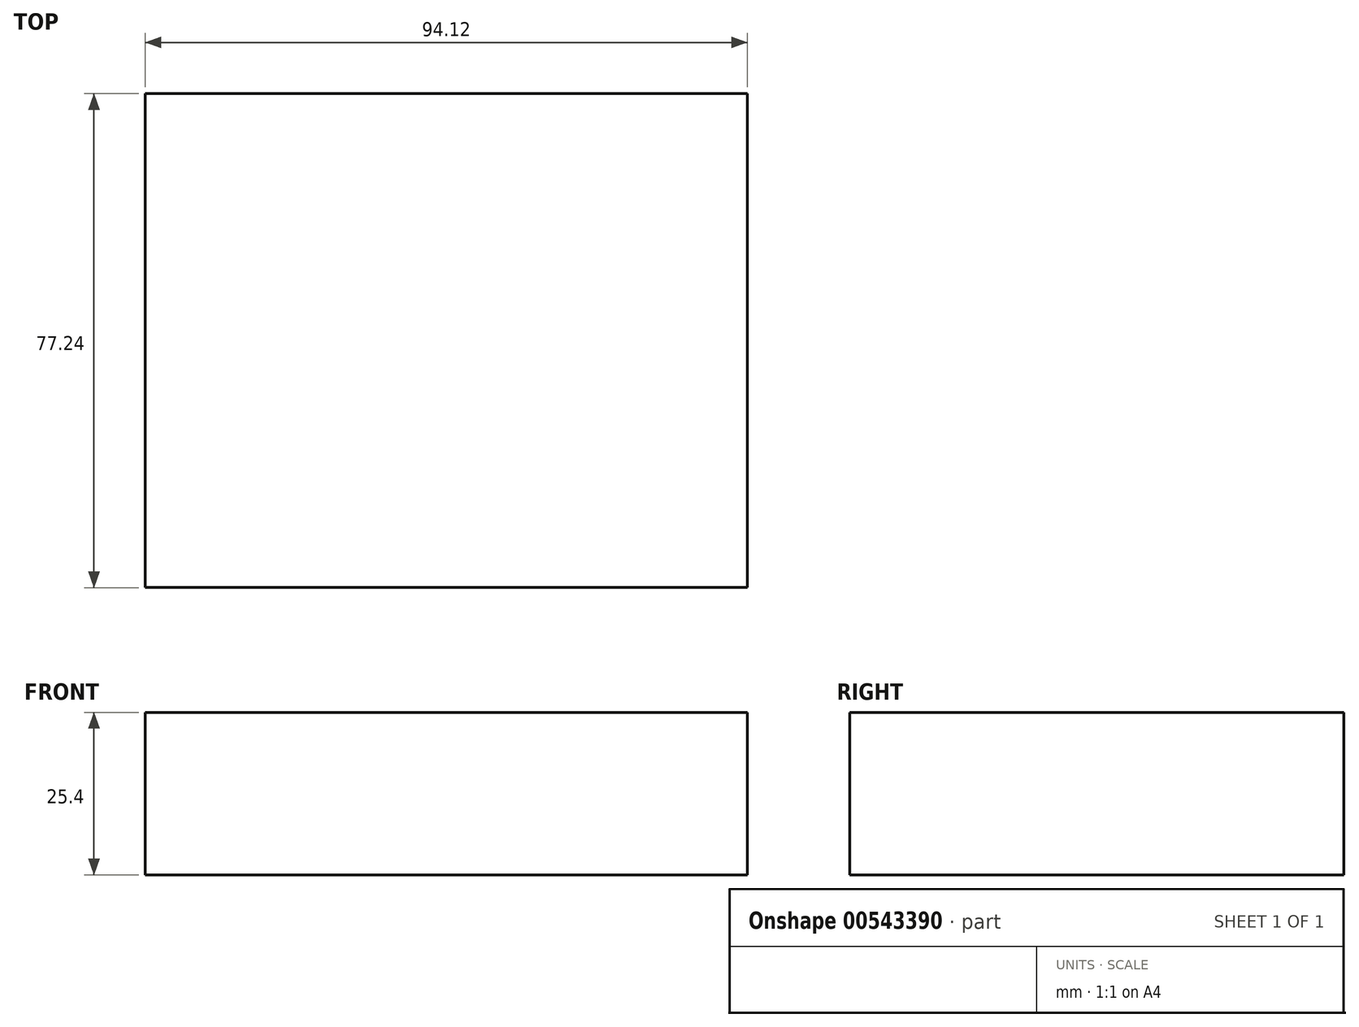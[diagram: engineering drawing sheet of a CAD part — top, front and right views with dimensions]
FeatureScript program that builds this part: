
annotation { "Feature Type Name" : "Feature", "Feature Type Description" : "" }
export const myFeature = defineFeature(function(context is Context, id is Id, definition is map)
    precondition{}
    {
        {
            var Q0;
            Q0=qCreatedBy(makeId("Top.planeOp"),FACE);
            var sketch = newSketch(context, id + "F0", { "sketchPlane" : qUnion([Q0])});
            skLineSegment(sketch, "E0.bottom", {"start": v(47.06, -38.62) * mm, "end": v(-47.06, -38.62) * mm});
            skLineSegment(sketch, "E0.top", {"start": v(47.06, 38.62) * mm, "end": v(-47.06, 38.62) * mm});
            skLineSegment(sketch, "E0.left", {"start": v(47.06, -38.62) * mm, "end": v(47.06, 38.62) * mm});
            skLineSegment(sketch, "E0.right", {"start": v(-47.06, -38.62) * mm, "end": v(-47.06, 38.62) * mm});
            skPoint(sketch, "E0.middle", {"position": v(0, 0) * mm});
            skSolve(sketch);
        }
        {
            var Q0;
            Q0=makeQuery(id+"F0.imprint","IMPRINT",FACE,{"disambiguationData":[TD([[makeQuery(id+"F0.imprint","IMPRINT",EDGE,{"derivedFrom":sQuery(id+"F0.wireOp",EDGE,"E0.bottom")}),-1.0]])]});
            extrude(context, id + "F1", {"entities" : qUnion([Q0]), "depth" : 25.4 * mm, "offsetDistance" : 25.4 * mm});
        }
    });
